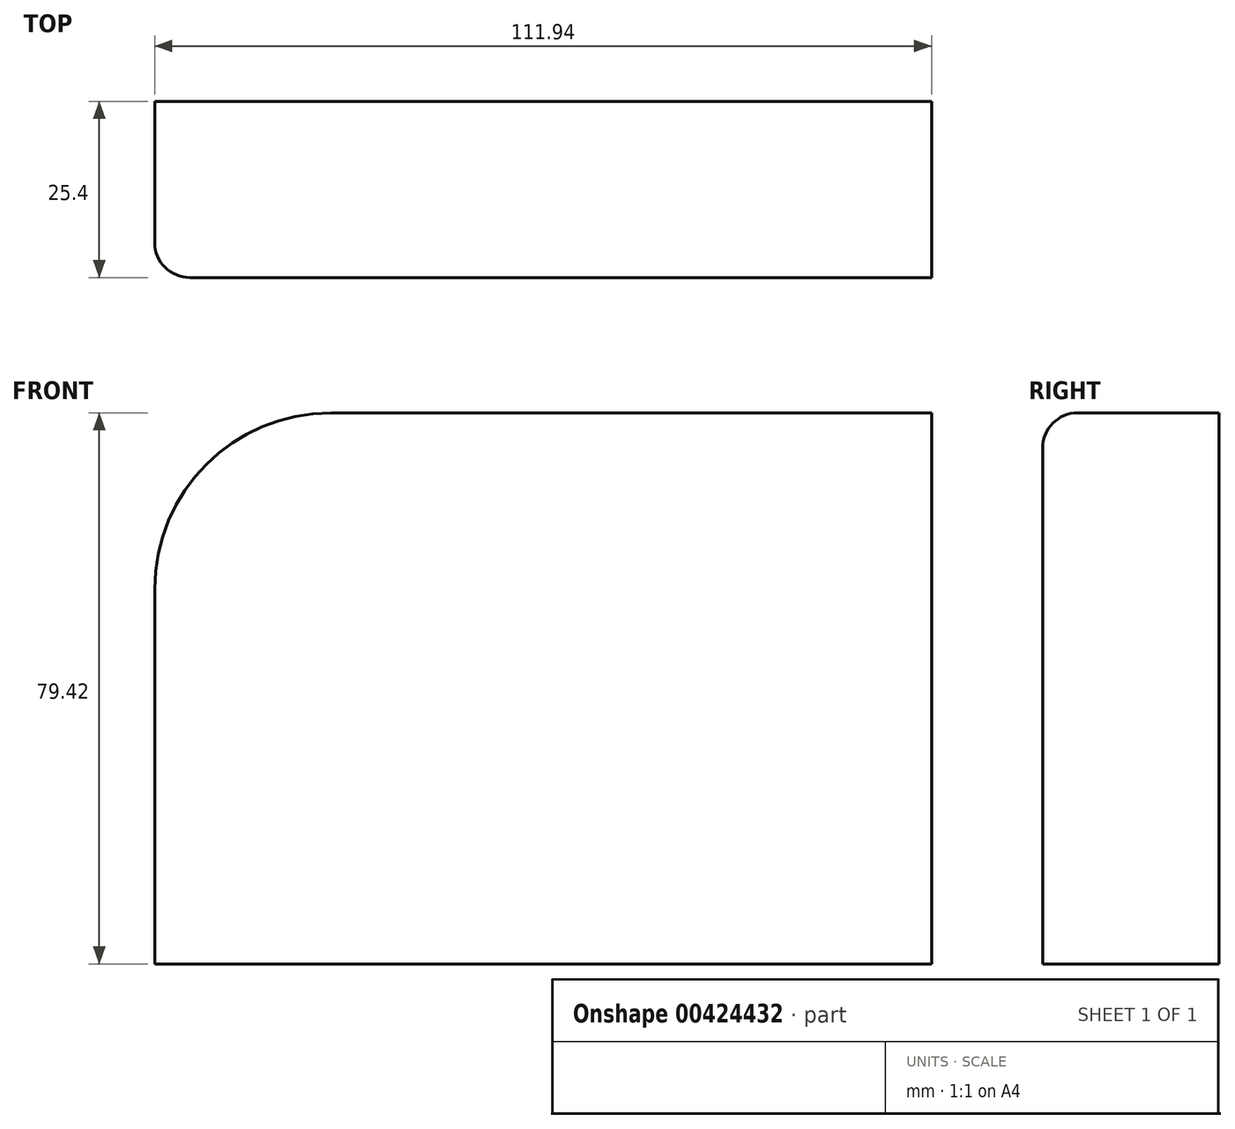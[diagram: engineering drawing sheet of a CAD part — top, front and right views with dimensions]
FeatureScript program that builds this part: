
annotation { "Feature Type Name" : "Feature", "Feature Type Description" : "" }
export const myFeature = defineFeature(function(context is Context, id is Id, definition is map)
    precondition{}
    {
        {
            var Q0;
            Q0=qCreatedBy(makeId("Front.planeOp"),FACE);
            var sketch = newSketch(context, id + "F0", { "sketchPlane" : qUnion([Q0])});
            skLineSegment(sketch, "E0.bottom", {"start": v(-30.57, 39.71) * mm, "end": v(55.97, 39.71) * mm});
            skLineSegment(sketch, "E0.top", {"start": v(-55.97, -39.71) * mm, "end": v(55.97, -39.71) * mm});
            skLineSegment(sketch, "E0.left", {"start": v(-55.97, 14.31) * mm, "end": v(-55.97, -39.71) * mm});
            skLineSegment(sketch, "E0.right", {"start": v(55.97, 39.71) * mm, "end": v(55.97, -39.71) * mm});
            skPoint(sketch, "E0.middle", {"position": v(0, 0) * mm});
            skPoint(sketch, "E1.visualSharp", {"position": v(-55.97, 39.71) * mm});
            skArc(sketch, "E1.filletArc", {"start": v(-30.57, 39.71) * mm, "mid": v(-48.53, 32.27) * mm, "end": v(-55.97, 14.31) * mm});
            skSolve(sketch);
        }
        {
            var Q0;
            Q0 = qSketchRegion(id + "F0", true);
            extrude(context, id + "F1", {"entities" : qUnion([Q0]), "depth" : 25.4 * mm});
        }
        {
            var Q0;
            Q0=makeQuery(id+"F1.opExtrude","CAP_EDGE",EDGE,{"disambiguationData":[OSD([sQuery(id+"F0.wireOp",EDGE,"E0.left")])],"isStart":false});
            fillet(context, id + "F2", {"entities" : qUnion([Q0]), "radius" : 5.08 * mm, "tangentPropagation" : true, "allowEdgeOverflow" : false});
        }
    });
